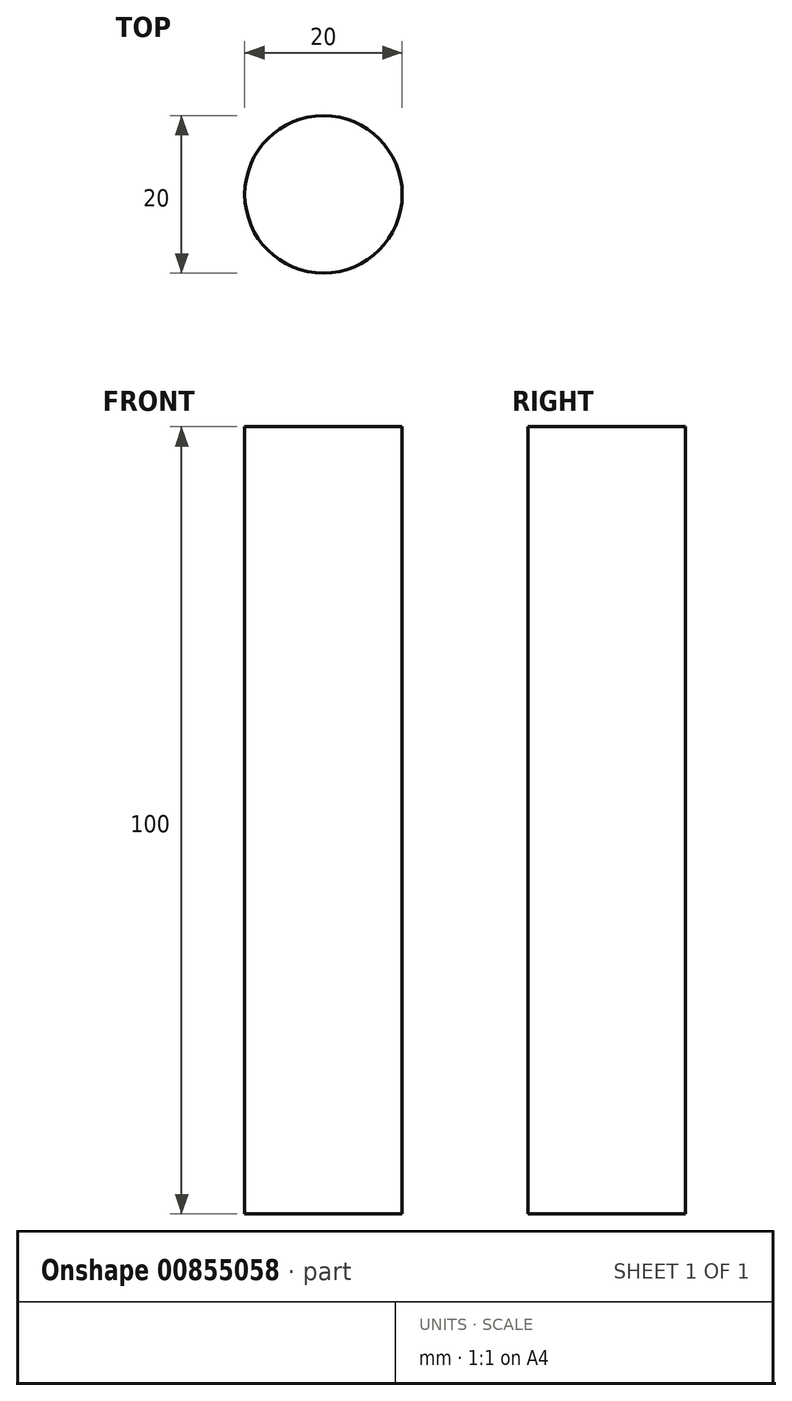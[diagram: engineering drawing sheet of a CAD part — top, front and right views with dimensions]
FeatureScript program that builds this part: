
annotation { "Feature Type Name" : "Feature", "Feature Type Description" : "" }
export const myFeature = defineFeature(function(context is Context, id is Id, definition is map)
    precondition{}
    {
        {
            var Q0;
            Q0=qCreatedBy(makeId("Top.planeOp"),FACE);
            var sketch = newSketch(context, id + "F0", { "sketchPlane" : qUnion([Q0])});
            skCircle(sketch, "E0", {"center": v(0, 0) * mm, "radius": 10 * mm});
            skSolve(sketch);
        }
        {
            var Q0;
            Q0=makeQuery(id+"F0.imprint","IMPRINT",FACE,{"disambiguationData":[TD([[makeQuery(id+"F0.imprint","IMPRINT",EDGE,{"derivedFrom":sQuery(id+"F0.wireOp",EDGE,"E0")}),1.0]])]});
            extrude(context, id + "F1", {"entities" : qUnion([Q0]), "depth" : 100 * mm, "offsetDistance" : 25 * mm});
        }
    });
